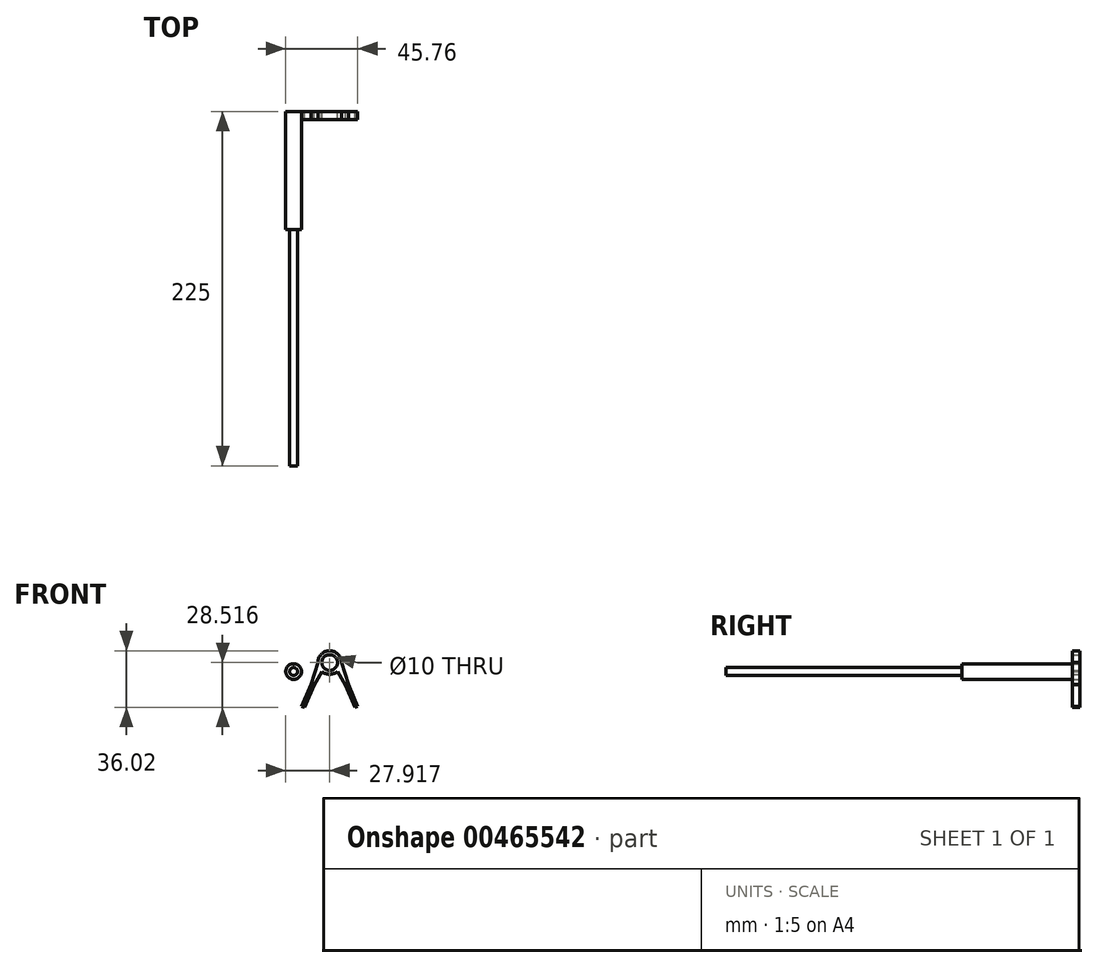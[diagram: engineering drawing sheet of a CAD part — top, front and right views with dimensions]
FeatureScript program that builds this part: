
annotation { "Feature Type Name" : "Feature", "Feature Type Description" : "" }
export const myFeature = defineFeature(function(context is Context, id is Id, definition is map)
    precondition{}
    {
        {
            var Q0;
            Q0=qCreatedBy(makeId("Front.planeOp"),FACE);
            var sketch = newSketch(context, id + "F0", { "sketchPlane" : qUnion([Q0])});
            skCircle(sketch, "E0", {"center": v(0, 0) * mm, "radius": 5 * mm});
            skSolve(sketch);
        }
        {
            var Q0;
            Q0=makeQuery(id+"F0.imprint","IMPRINT",FACE,{"disambiguationData":[TD([[makeQuery(id+"F0.imprint","IMPRINT",EDGE,{"derivedFrom":sQuery(id+"F0.wireOp",EDGE,"E0")}),1.0]])]});
            extrude(context, id + "F1", {"entities" : qUnion([Q0]), "depth" : 75 * mm});
        }
        {
            var Q0;
            Q0=makeQuery(id+"F1.opExtrude","CAP_FACE",FACE,{"disambiguationData":[OSD([sQuery(id+"F0.wireOp",EDGE,"E0")])],"isStart":false});
            var sketch = newSketch(context, id + "F2", { "sketchPlane" : qUnion([Q0])});
            skCircle(sketch, "E1", {"center": v(0, 0) * mm, "radius": 2.5 * mm});
            skSolve(sketch);
        }
        {
            var Q0;
            Q0=makeQuery(id+"F2.imprint","IMPRINT",FACE,{"disambiguationData":[TD([[makeQuery(id+"F2.imprint","IMPRINT",EDGE,{"derivedFrom":sQuery(id+"F2.wireOp",EDGE,"E1")}),1.0]])]});
            extrude(context, id + "F3", {"entities" : qUnion([Q0]), "operationType" : NewBodyOperationType.ADD, "depth" : 150 * mm});
        }
        {
            var Q0;
            Q0=qCreatedBy(makeId("Front.planeOp"),FACE);
            var sketch = newSketch(context, id + "F4", { "sketchPlane" : qUnion([Q0])});
            skLineSegment(sketch, "E2", {"start": v(22.92, 0) * mm, "end": v(22.92, -29.13) * mm, "construction": true});
            skLineSegment(sketch, "E3", {"start": v(22.92, -22.8) * mm, "end": v(38.92, -22.8) * mm, "construction": true});
            skLineSegment(sketch, "E4", {"start": v(22.92, -22.8) * mm, "end": v(6.92, -22.8) * mm, "construction": true});
            skLineSegment(sketch, "E5", {"start": v(22.92, -8.8) * mm, "end": v(32.92, -8.8) * mm, "construction": true});
            skLineSegment(sketch, "E6", {"start": v(22.92, -8.8) * mm, "end": v(12.92, -8.8) * mm, "construction": true});
            skLineSegment(sketch, "E7", {"start": v(22.92, 0) * mm, "end": v(22.92, 5.72) * mm, "construction": true});
            skCircle(sketch, "E8", {"center": v(22.92, 5.72) * mm, "radius": 7.5 * mm});
            skCircle(sketch, "E9", {"center": v(22.92, 5.72) * mm, "radius": 5 * mm});
            skLineSegment(sketch, "E10", {"start": v(27.77, 0) * mm, "end": v(32.92, -8.8) * mm});
            skLineSegment(sketch, "E11", {"start": v(32.92, -8.8) * mm, "end": v(38.92, -22.8) * mm});
            skLineSegment(sketch, "E12", {"start": v(38.92, -22.8) * mm, "end": v(40.76, -22.01) * mm});
            skLineSegment(sketch, "E13", {"start": v(40.76, -22.01) * mm, "end": v(34.76, -8.01) * mm});
            skLineSegment(sketch, "E14", {"start": v(34.76, -8.01) * mm, "end": v(32.92, -8.8) * mm, "construction": true});
            skLineSegment(sketch, "E15", {"start": v(34.76, -8.01) * mm, "end": v(30.42, 5.72) * mm});
            skLineSegment(sketch, "E16", {"start": v(18.06, 0) * mm, "end": v(12.92, -8.8) * mm});
            skLineSegment(sketch, "E17", {"start": v(12.92, -8.8) * mm, "end": v(6.92, -22.8) * mm});
            skLineSegment(sketch, "E18", {"start": v(6.92, -22.8) * mm, "end": v(5.08, -22.01) * mm});
            skLineSegment(sketch, "E19", {"start": v(5.08, -22.01) * mm, "end": v(11.08, -8.01) * mm});
            skLineSegment(sketch, "E20", {"start": v(11.08, -8.01) * mm, "end": v(15.42, 5.72) * mm});
            skSolve(sketch);
        }
        {
            var Q0;
            {var subQ0=sQuery(id+"F4.wireOp",EDGE,"E10");Q0=makeQuery(id+"F4.imprint","IMPRINT",FACE,{"disambiguationData":[TD([[makeQuery(id+"F4.imprint","IMPRINT",EDGE,{"derivedFrom":subQ0}),1.0]])]});}
            var Q1;
            {var subQ0=sQuery(id+"F4.wireOp",EDGE,"E16");Q1=makeQuery(id+"F4.imprint","IMPRINT",FACE,{"disambiguationData":[TD([[makeQuery(id+"F4.imprint","IMPRINT",EDGE,{"derivedFrom":subQ0}),-1.0]])]});}
            var Q2;
            Q2=makeQuery(id+"F4.imprint","IMPRINT",FACE,{"disambiguationData":[TD([[makeQuery(id+"F4.imprint","IMPRINT",EDGE,{"derivedFrom":sQuery(id+"F4.wireOp",EDGE,"E9")}),-1.0]])]});
            extrude(context, id + "F5", {"entities" : qUnion([Q0, Q1, Q2]), "depth" : 5 * mm});
        }
    });
